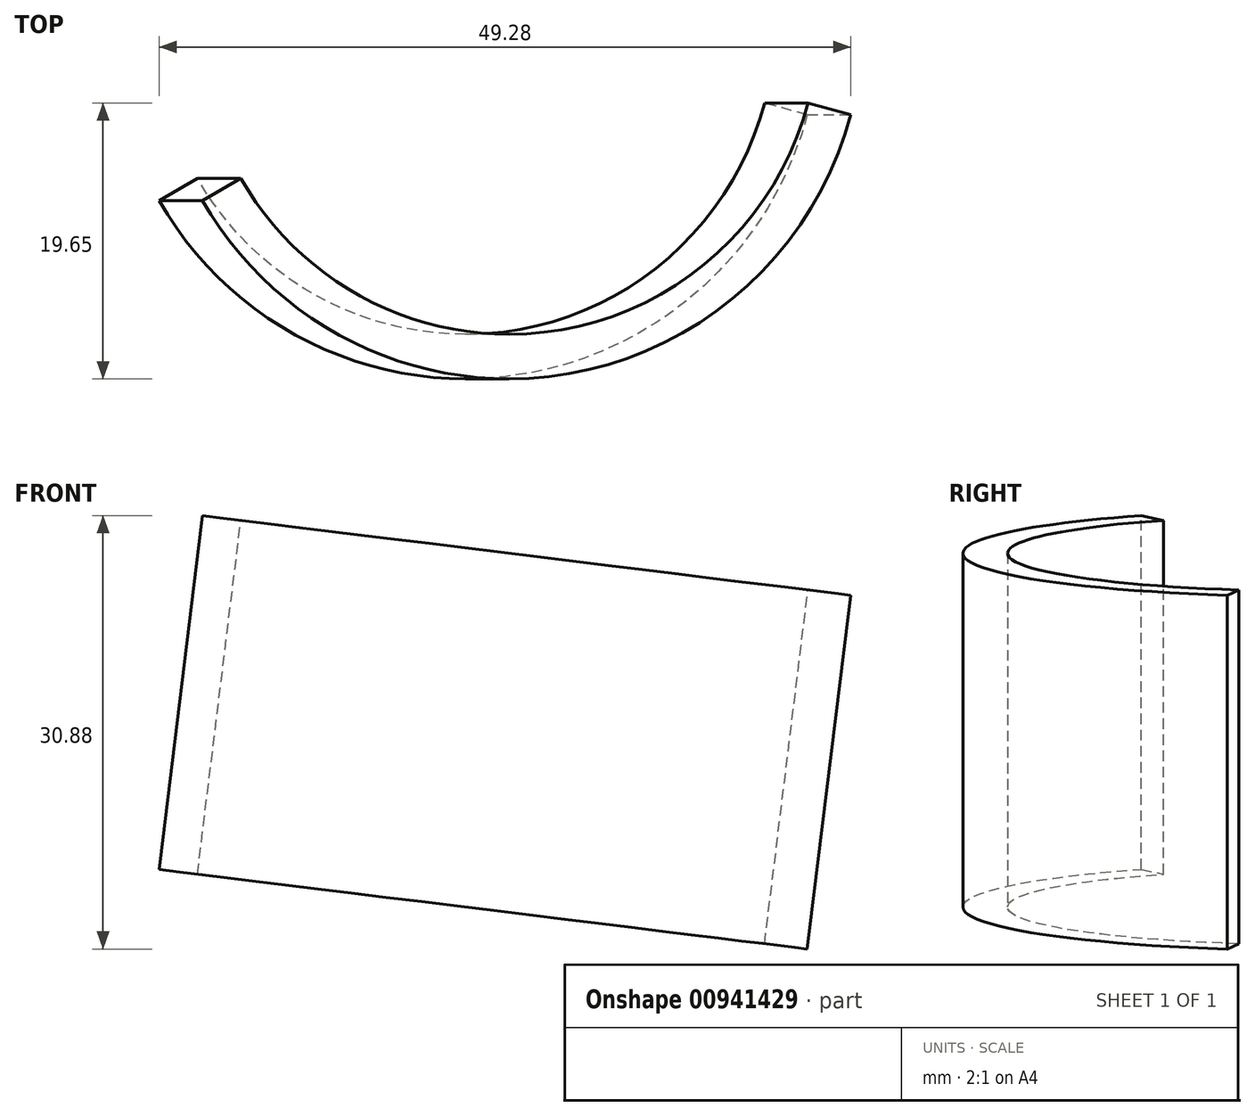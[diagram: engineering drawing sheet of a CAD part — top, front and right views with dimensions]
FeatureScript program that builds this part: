
annotation { "Feature Type Name" : "Feature", "Feature Type Description" : "" }
export const myFeature = defineFeature(function(context is Context, id is Id, definition is map)
    precondition{}
    {
        {
            var Q0;
            Q0=qCreatedBy(makeId("Front.planeOp"),FACE);
            var sketch = newSketch(context, id + "F0", { "sketchPlane" : qUnion([Q0])});
            skPoint(sketch, "E0.0", {"position": v(71.07, -68.97) * mm});
            skPoint(sketch, "E1.0", {"position": v(-68.63, -68.97) * mm});
            skPoint(sketch, "E2.0", {"position": v(1.22, -68.97) * mm});
            skLineSegment(sketch, "E3", {"start": v(71.07, -68.97) * mm, "end": v(13.92, -68.97) * mm});
            skLineSegment(sketch, "E4", {"start": v(13.92, -68.97) * mm, "end": v(17.01, -43.76) * mm});
            skLineSegment(sketch, "E5.0", {"start": v(-8.14, -66.26) * mm, "end": v(-5.05, -41.05) * mm});
            skLineSegment(sketch, "E6.0", {"start": v(-11.3, -65.88) * mm, "end": v(-8.2, -40.66) * mm});
            skLineSegment(sketch, "E7", {"start": v(-8.2, -40.66) * mm, "end": v(-5.05, -41.05) * mm});
            skLineSegment(sketch, "E8", {"start": v(-11.3, -65.88) * mm, "end": v(-8.14, -66.26) * mm});
            skLineSegment(sketch, "E9", {"start": v(71.07, -68.97) * mm, "end": v(-68.63, -68.97) * mm});
            skSolve(sketch);
        }
        {
            var Q0;
            Q0=makeQuery(id+"F0.imprint","IMPRINT",FACE,{"disambiguationData":[TD([[makeQuery(id+"F0.imprint","IMPRINT",EDGE,{"derivedFrom":sQuery(id+"F0.wireOp",EDGE,"E5.0")}),1.0]])]});
            var Q1;
            Q1=sQuery(id+"F0.wireOp",EDGE,"E4");
            revolve(context, id + "F1", {"surfaceOperationType" : NewSurfaceOperationType.NEW, "entities" : qUnion([Q0]), "axis" : qUnion([Q1]), "revolveType" : RevolveType.TWO_DIRECTIONS, "angle" : 165 * degree, "angleBack" : 30 * degree});
        }
    });
